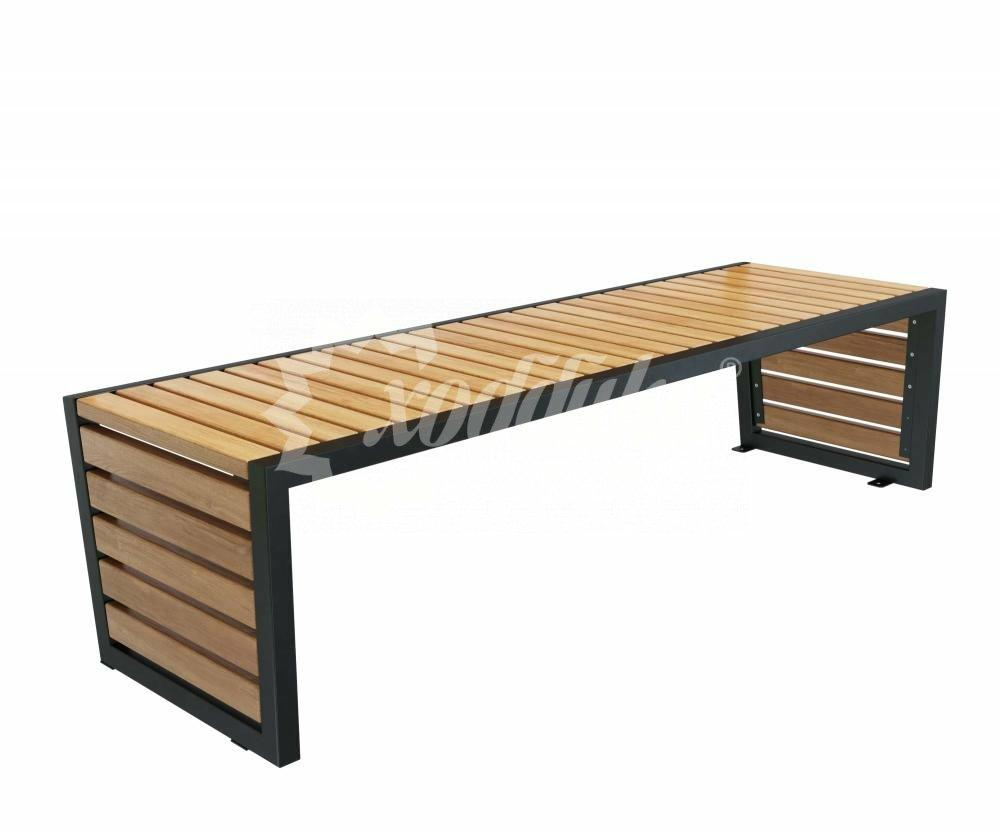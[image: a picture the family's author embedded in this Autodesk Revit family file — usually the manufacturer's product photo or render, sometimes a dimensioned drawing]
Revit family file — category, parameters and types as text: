
# Revit family: Скамейка стальная «Вижен» без спинки Арт 15078
name_source: partatom
category: Антураж
revit_build: Autodesk Revit 2018 (Build: 20180423_1000(x64)
units: mm (PartAtom-declared; Revit-internal decimal feet)

## family parameters
Всегда вертикально = Да
Источник визуального образа = Геометрия семейства
На основе рабочей плоскости = Нет
Общий = Нет
При загрузке вырезать с полостями = Нет
Точка расчета площади = Нет

## types (3) — shared parameters
URL = https://hobbyka.ru
Артикул товара = Арт. 15078
Высота = 450 мм
Группа модели = Скамейки
Изготовитель = ООО «Хоббика»
Изображение типоразмера = Скамейка стальная «Вижен» без спинки Арт 15078.jpg
Материал изделия = Сталь, дерево
Цвет каркаса = Сталь
Цвет лавки = Дерево
Ширина = 554 мм

## per-type parameters (varying)
| type | Версия 1,5 м | Версия 1,8 м | Версия 2,1 м | Длина | Описание |
| Версия 2,1 м | Нет | Нет | Да | 2100 мм | Скамейка стальная «Вижен» без спинки. Версия 2,1 м |
| Версия 1,8 м | Нет | Да | Нет | 1800 мм | Скамейка стальная «Вижен» без спинки. Версия 1,8 м |
| Версия 1,5 м | Да | Нет | Нет | 1500 мм | Скамейка стальная «Вижен» без спинки. Версия 1,5 м |
